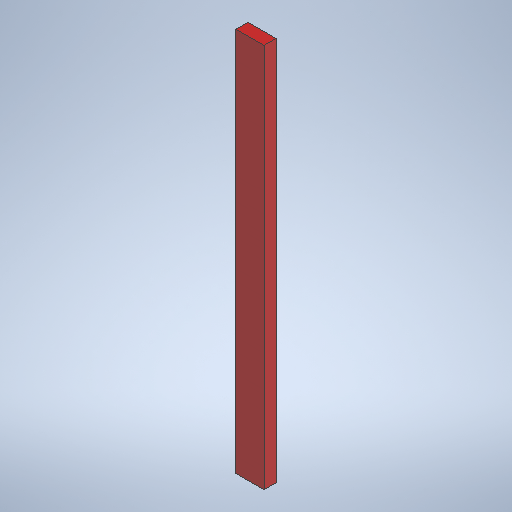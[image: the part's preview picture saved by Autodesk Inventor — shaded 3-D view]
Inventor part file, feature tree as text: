
AUTODESK INVENTOR PART (.ipt)
format: ipt  version: 2025.1 (Build 291241020, 241B)  size: 257,024 bytes
history: native  units: in
note: dims shown in document units (in); Inventor stores cm internally (conversion verified against a paired STEP export)
features: extrude x1, sketch x1, other x1
ambient origin geometry x8: Origin, YZ Plane, XZ Plane, XY Plane, X Axis, Y Axis, Z Axis, Center Point
bodies: Solid1 (feature_tree)
feature tree (3):
  extrude  "Extrusion1"  Depth=3.5in
  sketch  "Sketch1"  dims[d0=1.5in d1=3.5in d2=48.0in d3=0.0in]
  other  "Finish1"
